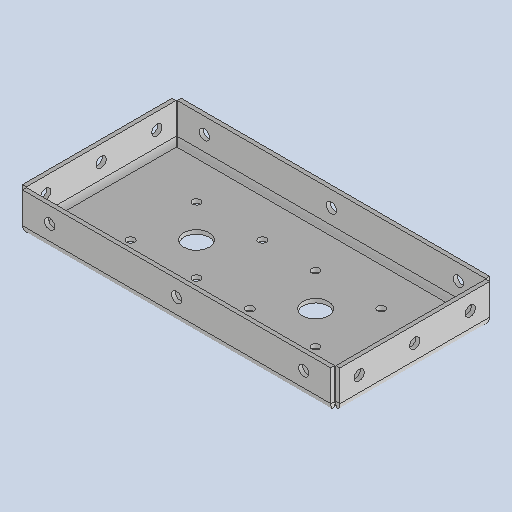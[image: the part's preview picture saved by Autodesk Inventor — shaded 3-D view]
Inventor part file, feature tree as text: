
AUTODESK INVENTOR PART (.ipt)
format: ipt  version: 2025 (Build 290162010, 162A)  size: 309,760 bytes
history: native  units: mm
features: sketch x5, sheet_metal_op x4, other x4, extrude x2, pattern_linear x2, projected_geometry x1
ambient origin geometry x8: Origin, YZ Plane, XZ Plane, XY Plane, X Axis, Y Axis, Z Axis, Center Point
bodies: Solid1 (feature_tree)
feature tree (18):
  sheet_metal_op  "Face1"
  sheet_metal_op  "Flange2"
  extrude  "Extrusion2"  Depth=400.0mm
  pattern_linear  "Rectangular Pattern1"  Count1=20  [1 undecoded]
  extrude  "Extrusion3"  Depth=5.0mm
  pattern_linear  "Rectangular Pattern2"  Count1=5 Spacing1=90.0deg
  sketch  "Sketch1"  dims[d2=5.0mm d25=400.0mm d26=200.0mm]
  other  "Plate1"
  sketch  "Sketch5"  dims[d27=5.0mm d28=2.5mm]
  other  "Plate3"
  sheet_metal_op  "Bend2"
  sheet_metal_op  "Corner2"
  sketch  "Sketch6"  dims[d29=10.0mm]
  sketch  "Sketch7"  dims[d30=6.0mm d31=50.0mm d32=90.0deg d33=6.0mm]
  projected_geometry  "Projected Loop2"
  sketch  "Sketch8"  dims[d34=20.0mm d35=1.0mm d36=6.0mm d37=32.0mm d38=150.0mm d39=5.0mm d40=0.0mm d41=13.0mm d42=25.0mm d43=0.0mm d44=0.0mm d45=30.0mm d47=160.0mm d48=13.0mm d49=25.0mm d50=0.0mm d51=0.0mm d52=30.0mm d54=70.0mm d55=10.0mm d56=83.0mm d57=83.0mm]
  other  "Cut1"
  other  "Definition1"
note: 1 required parameter value undecoded (feature->parameter linkage not recoverable at this tier; creation-order binding heuristic only, values carry confidence <= 0.55)
